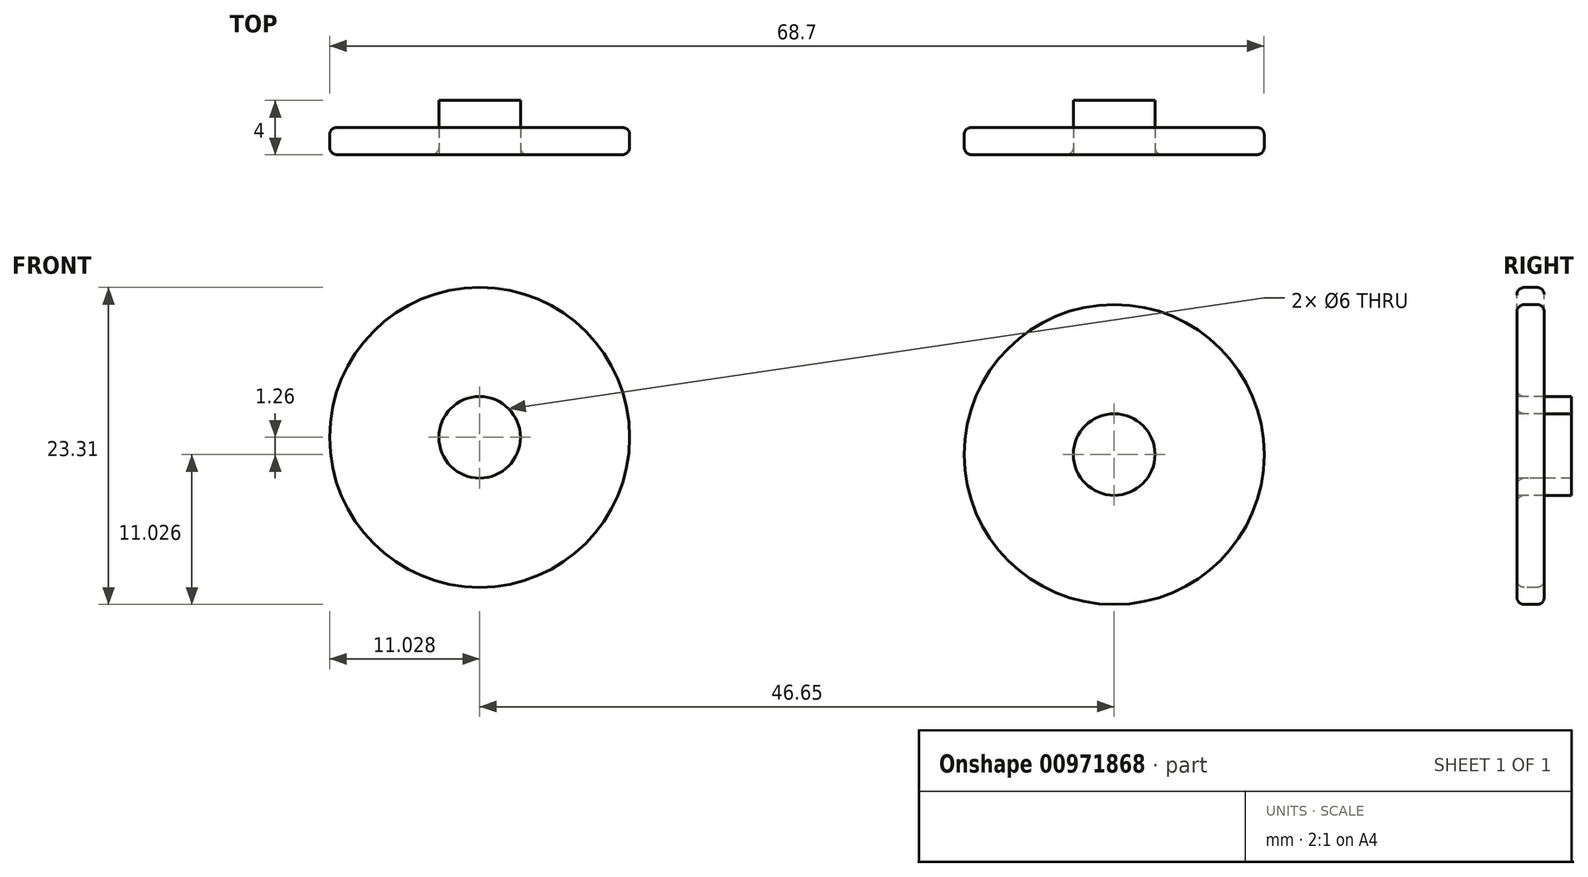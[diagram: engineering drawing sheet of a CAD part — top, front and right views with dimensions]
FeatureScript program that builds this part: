
annotation { "Feature Type Name" : "Feature", "Feature Type Description" : "" }
export const myFeature = defineFeature(function(context is Context, id is Id, definition is map)
    precondition{}
    {
        {
            var Q0;
            Q0=qCreatedBy(makeId("Front.planeOp"),FACE);
            var sketch = newSketch(context, id + "F0", { "sketchPlane" : qUnion([Q0])});
            skCircle(sketch, "E0", {"center": v(-66.5, 54.88) * mm, "radius": 11.03 * mm});
            skCircle(sketch, "E1", {"center": v(-19.84, 53.62) * mm, "radius": 11.03 * mm});
            skCircle(sketch, "E2", {"center": v(-66.5, 54.88) * mm, "radius": 3 * mm});
            skCircle(sketch, "E3", {"center": v(-19.84, 53.62) * mm, "radius": 3 * mm});
            skCircle(sketch, "E4", {"center": v(-65.65, 19.72) * mm, "radius": 11.03 * mm});
            skCircle(sketch, "E5", {"center": v(-19, 18.46) * mm, "radius": 11.03 * mm});
            skCircle(sketch, "E6", {"center": v(-65.65, 19.72) * mm, "radius": 3 * mm});
            skCircle(sketch, "E7", {"center": v(-19, 18.46) * mm, "radius": 3 * mm});
            skSolve(sketch);
        }
        {
            var Q0;
            Q0=makeQuery(id+"F0.imprint","IMPRINT",FACE,{"disambiguationData":[TD([[makeQuery(id+"F0.imprint","IMPRINT",EDGE,{"derivedFrom":sQuery(id+"F0.wireOp",EDGE,"E1")}),1.0]])]});
            var Q1;
            Q1=makeQuery(id+"F0.imprint","IMPRINT",FACE,{"disambiguationData":[TD([[makeQuery(id+"F0.imprint","IMPRINT",EDGE,{"derivedFrom":sQuery(id+"F0.wireOp",EDGE,"E0")}),1.0]])]});
            extrude(context, id + "F1", {"entities" : qUnion([Q0, Q1]), "depth" : -2 * mm, "offsetDistance" : 25.4 * mm});
        }
        {
            var Q0;
            Q0=makeQuery(id+"F1.opExtrude","CAP_EDGE",EDGE,{"disambiguationData":[OSD([sQuery(id+"F0.wireOp",EDGE,"E1")])],"isStart":false});
            var Q1;
            Q1=makeQuery(id+"F1.opExtrude","CAP_EDGE",EDGE,{"disambiguationData":[OSD([sQuery(id+"F0.wireOp",EDGE,"E0")])],"isStart":false});
            fillet(context, id + "F2", {"entities" : qUnion([Q0, Q1]), "radius" : .5 * mm, "tangentPropagation" : true, "allowEdgeOverflow" : false});
        }
        {
            var Q0;
            Q0=makeQuery(id+"F0.imprint","IMPRINT",FACE,{"disambiguationData":[TD([[makeQuery(id+"F0.imprint","IMPRINT",EDGE,{"derivedFrom":sQuery(id+"F0.wireOp",EDGE,"E2")}),1.0]])]});
            var Q1;
            Q1=makeQuery(id+"F0.imprint","IMPRINT",FACE,{"disambiguationData":[TD([[makeQuery(id+"F0.imprint","IMPRINT",EDGE,{"derivedFrom":sQuery(id+"F0.wireOp",EDGE,"E3")}),1.0]])]});
            extrude(context, id + "F3", {"entities" : qUnion([Q0, Q1]), "depth" : -4 * mm, "offsetDistance" : 25.4 * mm});
        }
        {
            var Q0;
            Q0=makeQuery(id+"F1.opExtrude","CAP_FACE",FACE,{"disambiguationData":[OSD([sQuery(id+"F0.wireOp",EDGE,"E0"),sQuery(id+"F0.wireOp",EDGE,"E2")])],"isStart":true});
            var Q1;
            Q1=makeQuery(id+"F1.opExtrude","CAP_FACE",FACE,{"disambiguationData":[OSD([sQuery(id+"F0.wireOp",EDGE,"E1"),sQuery(id+"F0.wireOp",EDGE,"E3")])],"isStart":true});
            fillet(context, id + "F4", {"entities" : qUnion([Q0, Q1]), "radius" : .55 * mm, "tangentPropagation" : true, "allowEdgeOverflow" : false});
        }
    });
